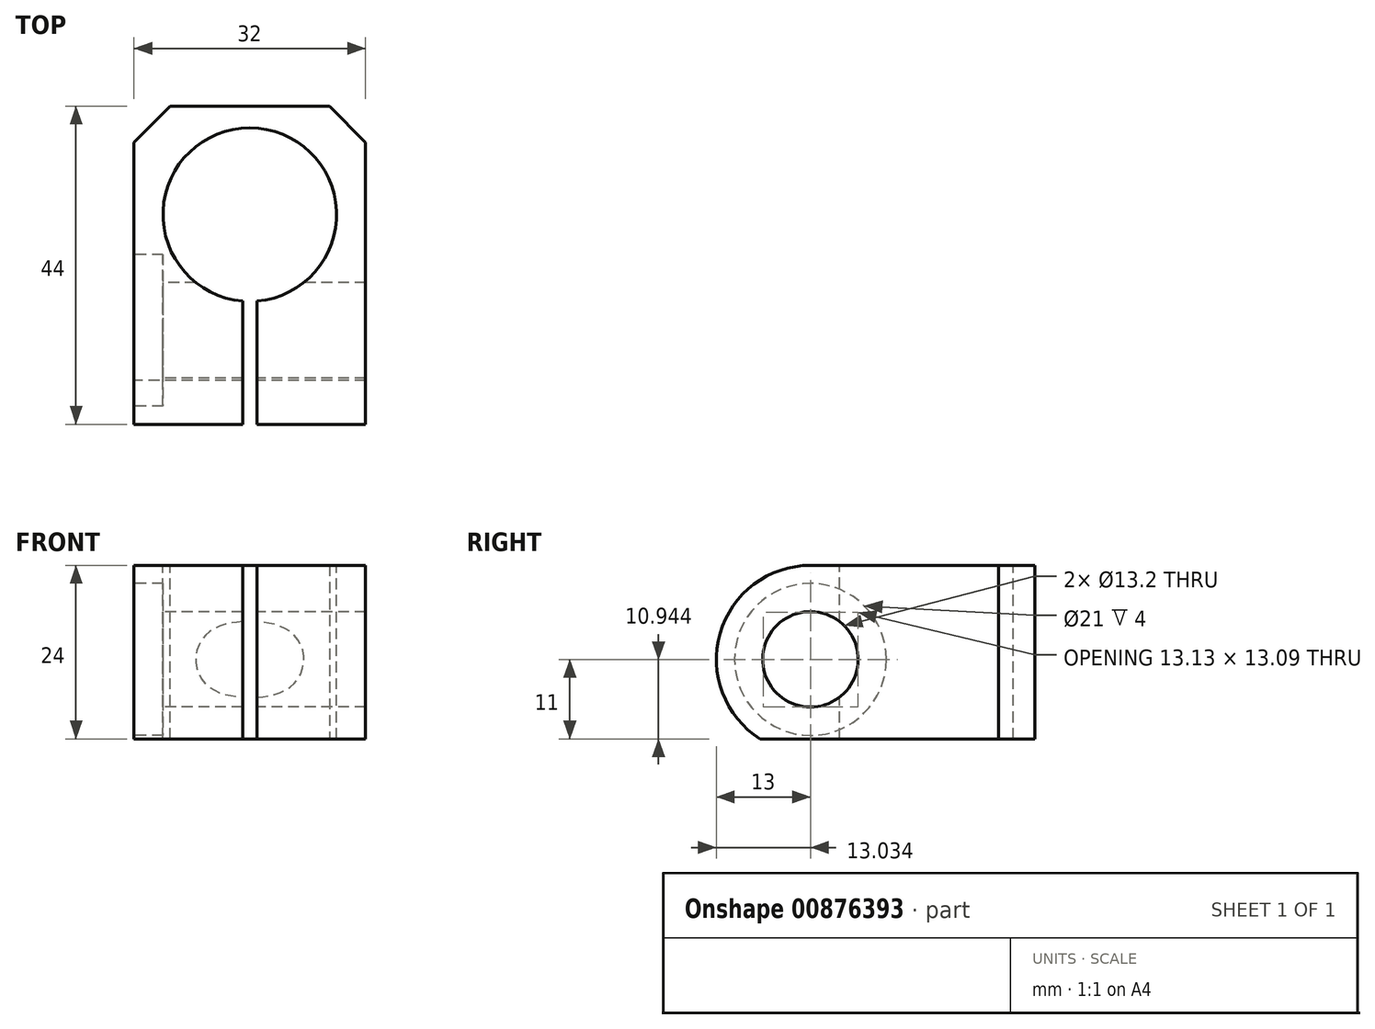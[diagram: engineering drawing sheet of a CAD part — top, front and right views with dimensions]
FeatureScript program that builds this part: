
annotation { "Feature Type Name" : "Feature", "Feature Type Description" : "" }
export const myFeature = defineFeature(function(context is Context, id is Id, definition is map)
    precondition{}
    {
        {
            var Q0;
            Q0=qCreatedBy(makeId("Right.planeOp"),FACE);
            var sketch = newSketch(context, id + "F0", { "sketchPlane" : qUnion([Q0])});
            skArc(sketch, "E0", {"start": v(0, 13) * mm, "mid": v(-12.49, 3.6) * mm, "end": v(-6.93, -11) * mm});
            skLineSegment(sketch, "E1", {"start": v(0, 13) * mm, "end": v(31, 13) * mm});
            skLineSegment(sketch, "E2", {"start": v(31, 13) * mm, "end": v(31, -11) * mm});
            skLineSegment(sketch, "E3", {"start": v(31, -11) * mm, "end": v(-6.93, -11) * mm});
            skCircle(sketch, "E4", {"center": v(0, 0) * mm, "radius": 6.6 * mm});
            skSolve(sketch);
        }
        {
            var Q0;
            Q0=qCreatedBy(makeId("Top.planeOp"),FACE);
            var sketch = newSketch(context, id + "F1", { "sketchPlane" : qUnion([Q0])});
            skLineSegment(sketch, "E5.top", {"start": v(1, -13) * mm, "end": v(-1, -13) * mm});
            skArc(sketch, "E6", {"start": v(1, 4.04) * mm, "mid": v(0, 28) * mm, "end": v(-1, 4.04) * mm});
            skLineSegment(sketch, "E7", {"start": v(-1, -13) * mm, "end": v(-1, 4.04) * mm});
            skLineSegment(sketch, "E8", {"start": v(1, -13) * mm, "end": v(1, 4.04) * mm});
            skSolve(sketch);
        }
        {
            var Q0;
            Q0=makeQuery(id+"F0.imprint","IMPRINT",FACE,{"disambiguationData":[TD([[makeQuery(id+"F0.imprint","IMPRINT",EDGE,{"derivedFrom":sQuery(id+"F0.wireOp",EDGE,"E0")}),1.0]])]});
            extrude(context, id + "F2", {"entities" : qUnion([Q0]), "endBound" : BoundingType.SYMMETRIC, "depth" : 32 * mm, "offsetDistance" : 25 * mm});
        }
        {
            var Q0;
            Q0=makeQuery(id+"F2.opExtrude","CAP_FACE",FACE,{"disambiguationData":[OSD([sQuery(id+"F0.wireOp",EDGE,"E0"),sQuery(id+"F0.wireOp",EDGE,"E1"),sQuery(id+"F0.wireOp",EDGE,"E2"),sQuery(id+"F0.wireOp",EDGE,"E3"),sQuery(id+"F0.wireOp",EDGE,"E4")])],"isStart":true});
            var sketch = newSketch(context, id + "F3", { "sketchPlane" : qUnion([Q0])});
            skCircle(sketch, "E9", {"center": v(0, 0) * mm, "radius": 10.5 * mm});
            skSolve(sketch);
        }
        {
            var Q0;
            Q0=makeQuery(id+"F3.imprint","IMPRINT",FACE,{"disambiguationData":[TD([[makeQuery(id+"F3.imprint","IMPRINT",EDGE,{"derivedFrom":sQuery(id+"F3.wireOp",EDGE,"E9")}),1.0]])]});
            extrude(context, id + "F4", {"entities" : qUnion([Q0]), "operationType" : NewBodyOperationType.REMOVE, "oppositeDirection" : true, "depth" : 4 * mm, "offsetDistance" : 25 * mm});
        }
        {
            var Q0;
            Q0=makeQuery(id+"F1.imprint","IMPRINT",FACE,{"disambiguationData":[TD([[makeQuery(id+"F1.imprint","IMPRINT",EDGE,{"derivedFrom":sQuery(id+"F1.wireOp",EDGE,"E5.top")}),-1.0]])]});
            extrude(context, id + "F5", {"entities" : qUnion([Q0]), "operationType" : NewBodyOperationType.REMOVE, "endBound" : BoundingType.SYMMETRIC, "oppositeDirection" : true, "depth" : 30 * mm, "offsetDistance" : 25 * mm});
        }
        {
            var Q0;
            Q0=makeQuery(id+"F2.opExtrude","CAP_EDGE",EDGE,{"disambiguationData":[OSD([sQuery(id+"F0.wireOp",EDGE,"E2")])],"isStart":false});
            var Q1;
            Q1=makeQuery(id+"F2.opExtrude","CAP_EDGE",EDGE,{"disambiguationData":[OSD([sQuery(id+"F0.wireOp",EDGE,"E2")])],"isStart":true});
            chamfer(context, id + "F6", {"entities" : qUnion([Q0, Q1]), "width" : 5 * mm, "tangentPropagation" : true});
        }
    });
